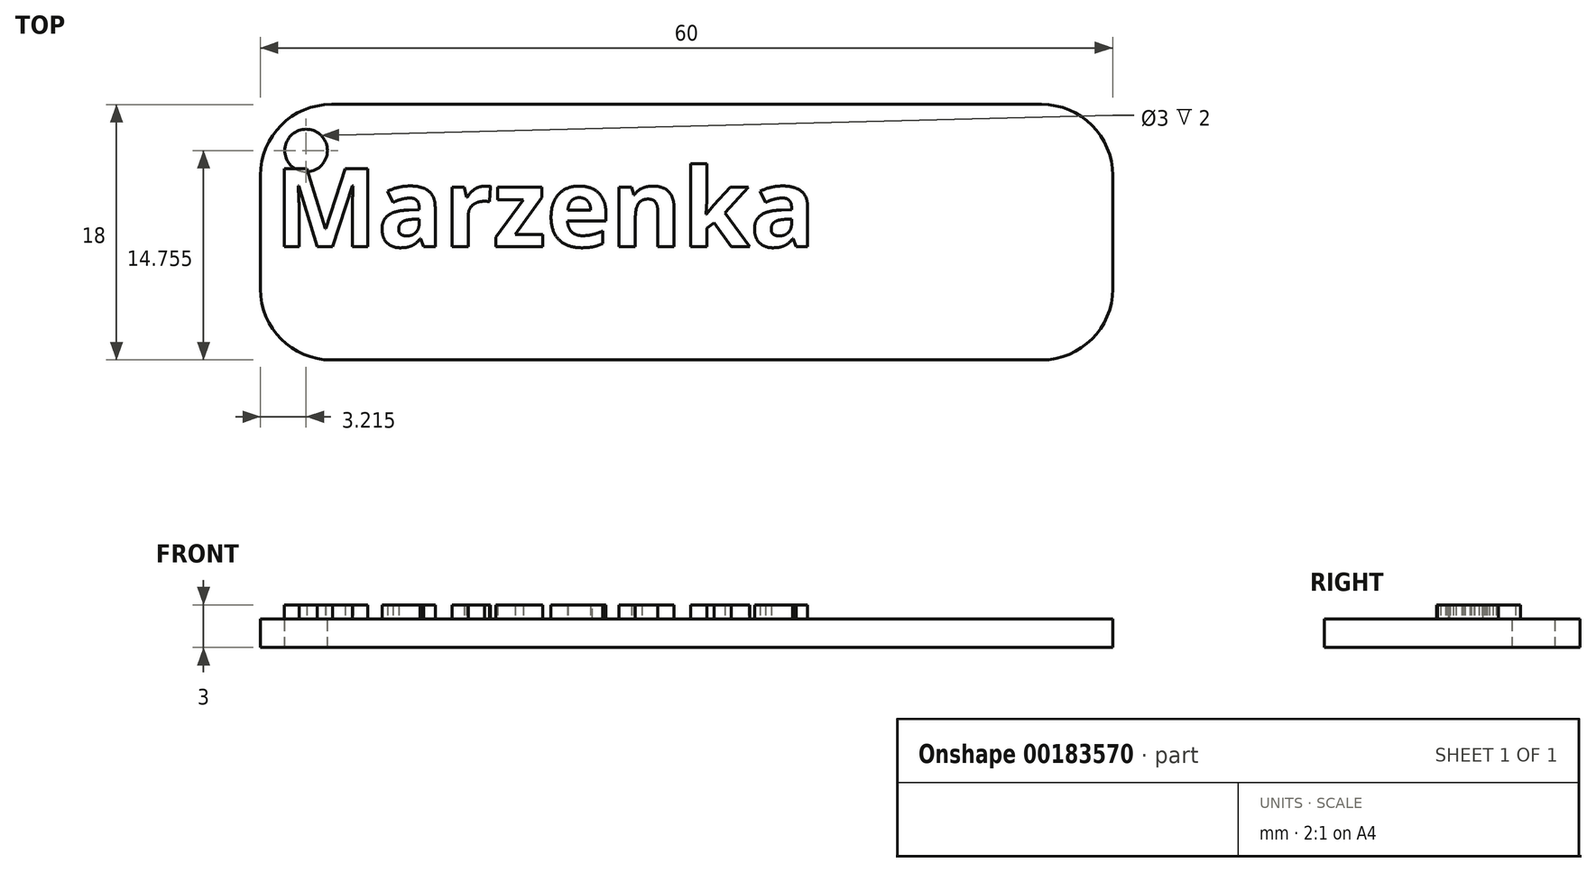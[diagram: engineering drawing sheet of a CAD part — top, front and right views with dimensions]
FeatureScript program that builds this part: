
annotation { "Feature Type Name" : "Feature", "Feature Type Description" : "" }
export const myFeature = defineFeature(function(context is Context, id is Id, definition is map)
    precondition{}
    {
        {
            var Q0;
            Q0=qCreatedBy(makeId("Top.planeOp"),FACE);
            var sketch = newSketch(context, id + "F0", { "sketchPlane" : qUnion([Q0])});
            skLineSegment(sketch, "E0.bottom", {"start": v(-19.56, 7.88) * mm, "end": v(40.44, 7.88) * mm});
            skLineSegment(sketch, "E0.top", {"start": v(-19.56, -10.12) * mm, "end": v(40.44, -10.12) * mm});
            skLineSegment(sketch, "E0.left", {"start": v(-19.56, 7.88) * mm, "end": v(-19.56, -10.12) * mm});
            skLineSegment(sketch, "E0.right", {"start": v(40.44, 7.88) * mm, "end": v(40.44, -10.12) * mm});
            skSolve(sketch);
        }
        {
            var Q0;
            Q0=makeQuery(id+"F0.imprint","IMPRINT",FACE,{"disambiguationData":[TD([[makeQuery(id+"F0.imprint","IMPRINT",EDGE,{"derivedFrom":sQuery(id+"F0.wireOp",EDGE,"E0.bottom")}),-1.0]])]});
            extrude(context, id + "F1", {"entities" : qUnion([Q0]), "depth" : 2 * mm});
        }
        {
            var Q0;
            Q0=makeQuery(id+"F1.opExtrude","CAP_FACE",FACE,{"disambiguationData":[OSD([sQuery(id+"F0.wireOp",EDGE,"E0.bottom"),sQuery(id+"F0.wireOp",EDGE,"E0.top"),sQuery(id+"F0.wireOp",EDGE,"E0.left"),sQuery(id+"F0.wireOp",EDGE,"E0.right")])],"isStart":false});
            var sketch = newSketch(context, id + "F2", { "sketchPlane" : qUnion([Q0])});
            skText(sketch, "E1", { "text": "Marzenka\n", "fontName": "OpenSans-Bold.ttf"});
            const initialGuessF2  = {"E1": [-0.01856, -0.00214, 1, 0, 0.00553]};
            skSetInitialGuess(sketch, initialGuessF2);
            skSolve(sketch);
        }
        {
            var Q0;
            Q0=makeQuery(id+"F1.opExtrude","SWEPT_EDGE",EDGE,{"disambiguationData":[OSD([sQuery(id+"F0.wireOp",EDGE,"E0.top"),sQuery(id+"F0.wireOp",EDGE,"E0.left")])]});
            var Q1;
            Q1=makeQuery(id+"F1.opExtrude","SWEPT_EDGE",EDGE,{"disambiguationData":[OSD([sQuery(id+"F0.wireOp",EDGE,"E0.top"),sQuery(id+"F0.wireOp",EDGE,"E0.right")])]});
            var Q2;
            Q2=makeQuery(id+"F1.opExtrude","SWEPT_EDGE",EDGE,{"disambiguationData":[OSD([sQuery(id+"F0.wireOp",EDGE,"E0.bottom"),sQuery(id+"F0.wireOp",EDGE,"E0.right")])]});
            var Q3;
            Q3=makeQuery(id+"F1.opExtrude","SWEPT_EDGE",EDGE,{"disambiguationData":[OSD([sQuery(id+"F0.wireOp",EDGE,"E0.bottom"),sQuery(id+"F0.wireOp",EDGE,"E0.left")])]});
            fillet(context, id + "F3", {"entities" : qUnion([Q0, Q1, Q2, Q3]), "radius" : 5 * mm, "tangentPropagation" : true, "allowEdgeOverflow" : false});
        }
        {
            var Q0;
            {var subQ0=sQuery(id+"F0.wireOp",EDGE,"E0.bottom");var subQ1=sQuery(id+"F0.wireOp",EDGE,"E0.top");var subQ2=sQuery(id+"F0.wireOp",EDGE,"E0.left");var subQ3=sQuery(id+"F0.wireOp",EDGE,"E0.right");Q0=makeQuery(id+"Fny4Zjm7x0LKICa_1.boolean.opBoolean","SPLIT",FACE,{"disambiguationData":[TD([makeQuery(id+"F1.opExtrude","SWEPT_FACE",FACE,{"disambiguationData":[OSD([subQ0])]})])],"derivedFrom":makeQuery(id+"F1.opExtrude","CAP_FACE",FACE,{"disambiguationData":[OSD([subQ0,subQ1,subQ2,subQ3])],"isStart":false})});}
            var sketch = newSketch(context, id + "F4", { "sketchPlane" : qUnion([Q0])});
            skCircle(sketch, "E2", {"center": v(-16.34, 4.63) * mm, "radius": 1.5 * mm});
            skSolve(sketch);
        }
        {
            var Q0;
            Q0=makeQuery(id+"F4.imprint","IMPRINT",FACE,{"disambiguationData":[TD([[makeQuery(id+"F4.imprint","IMPRINT",EDGE,{"derivedFrom":sQuery(id+"F4.wireOp",EDGE,"E2")}),1.0]])]});
            extrude(context, id + "F5", {"entities" : qUnion([Q0]), "operationType" : NewBodyOperationType.REMOVE, "oppositeDirection" : true, "depth" : 25 * mm});
        }
        {
            var Q0;
            Q0 = qSketchRegion(id + "F2", true);
            extrude(context, id + "F6", {"entities" : qUnion([Q0]), "operationType" : NewBodyOperationType.ADD, "depth" : 1 * mm});
        }
    });
